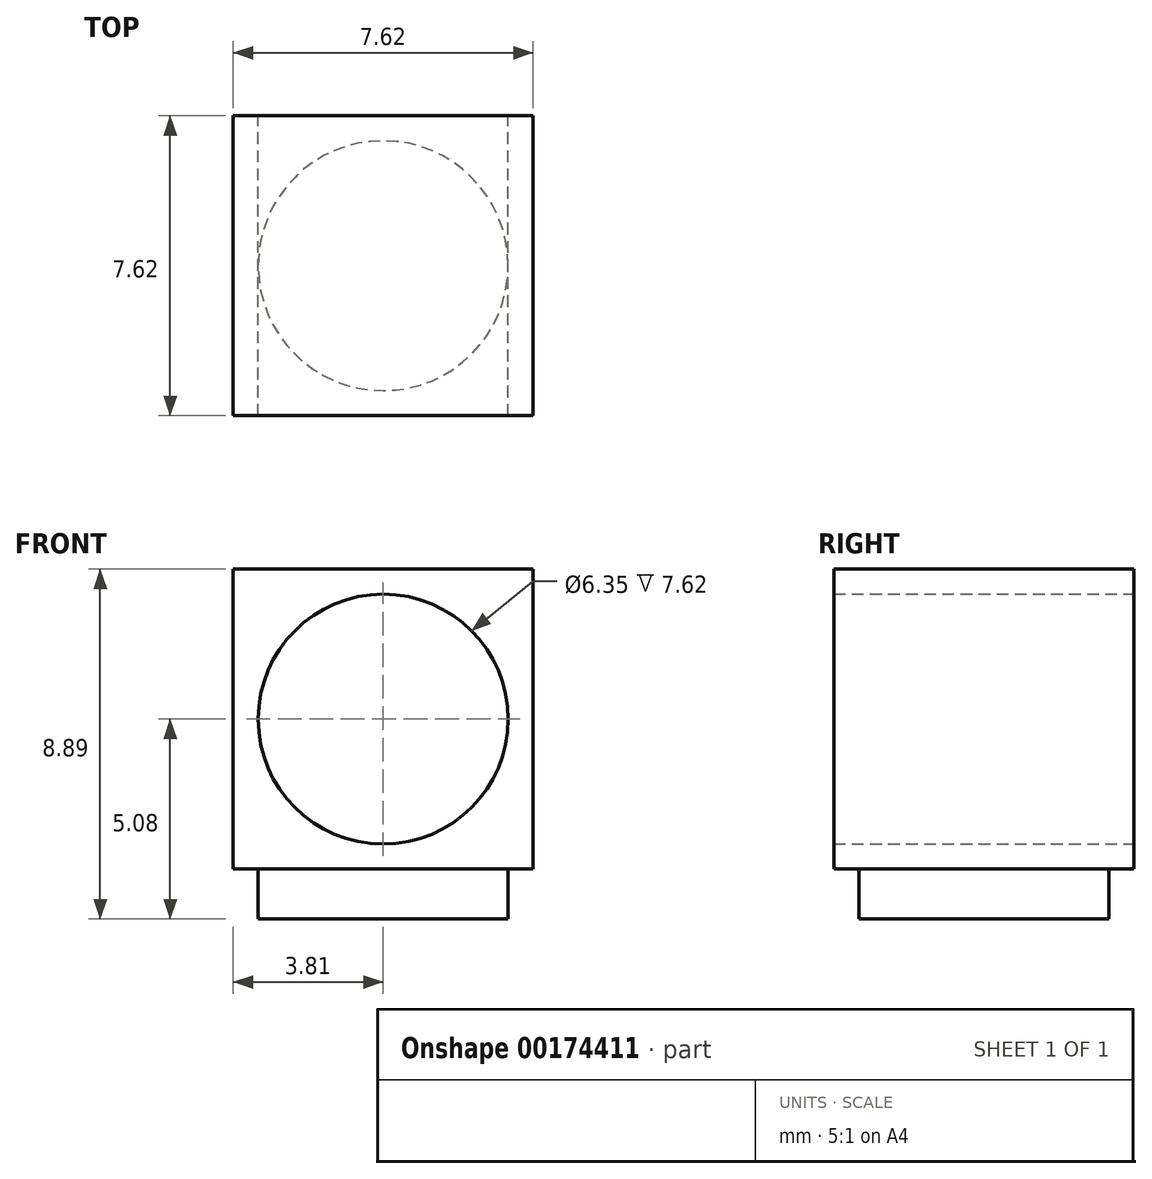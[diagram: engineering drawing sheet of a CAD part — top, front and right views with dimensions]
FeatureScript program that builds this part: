
annotation { "Feature Type Name" : "Feature", "Feature Type Description" : "" }
export const myFeature = defineFeature(function(context is Context, id is Id, definition is map)
    precondition{}
    {
        {
            var Q0;
            Q0=qCreatedBy(makeId("Front.planeOp"),FACE);
            var sketch = newSketch(context, id + "F0", { "sketchPlane" : qUnion([Q0])});
            skLineSegment(sketch, "E0.bottom", {"start": v(3.8, 3.81) * mm, "end": v(-3.81, 3.81) * mm});
            skLineSegment(sketch, "E0.top", {"start": v(3.81, -3.8) * mm, "end": v(-3.81, -3.8) * mm});
            skLineSegment(sketch, "E0.left", {"start": v(3.8, 3.81) * mm, "end": v(3.8, -3.8) * mm});
            skLineSegment(sketch, "E0.right", {"start": v(-3.81, 3.81) * mm, "end": v(-3.81, -3.8) * mm});
            skPoint(sketch, "E0.middle", {"position": v(0, 0) * mm});
            skCircle(sketch, "E1", {"center": v(0, 0) * mm, "radius": 3.18 * mm});
            skSolve(sketch);
        }
        {
            var Q0;
            Q0 = qSketchRegion(id + "F0", true);
            extrude(context, id + "F1", {"entities" : qUnion([Q0]), "depth" : 7.62 * mm, "offsetDistance" : 25.4 * mm});
        }
        {
            var Q0;
            Q0=makeQuery(id+"F1.opExtrude","SWEPT_FACE",FACE,{"disambiguationData":[OSD([sQuery(id+"F0.wireOp",EDGE,"E0.top")])]});
            var sketch = newSketch(context, id + "F2", { "sketchPlane" : qUnion([Q0])});
            skCircle(sketch, "E2", {"center": v(0, 3.81) * mm, "radius": 3.18 * mm});
            skPoint(sketch, "E2.centerSnap0", {"position": v(3.8, 3.81) * mm});
            skSolve(sketch);
        }
        {
            var Q0;
            Q0 = qSketchRegion(id + "F2", true);
            extrude(context, id + "F3", {"entities" : qUnion([Q0]), "operationType" : NewBodyOperationType.ADD, "depth" : 1.27 * mm, "offsetDistance" : 25.4 * mm});
        }
    });
